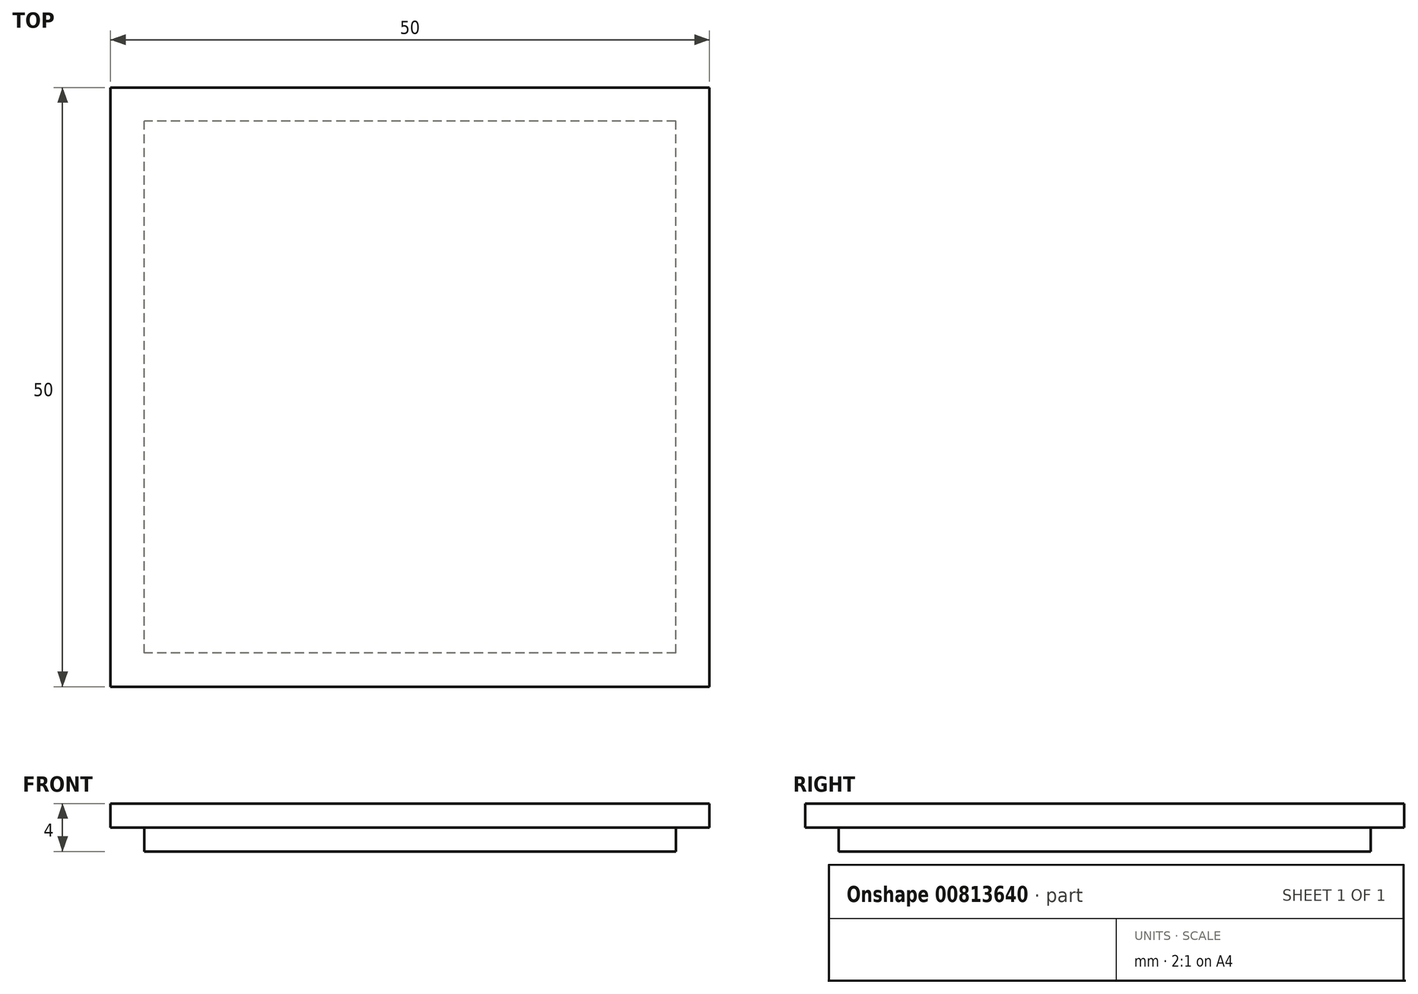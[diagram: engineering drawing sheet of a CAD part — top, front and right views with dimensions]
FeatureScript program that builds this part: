
annotation { "Feature Type Name" : "Feature", "Feature Type Description" : "" }
export const myFeature = defineFeature(function(context is Context, id is Id, definition is map)
    precondition{}
    {
        {
            var Q0;
            Q0=qCreatedBy(makeId("Top.planeOp"),FACE);
            var sketch = newSketch(context, id + "F0", { "sketchPlane" : qUnion([Q0])});
            skLineSegment(sketch, "E0.bottom", {"start": v(25, 25) * mm, "end": v(-25, 25) * mm});
            skLineSegment(sketch, "E0.top", {"start": v(25, -25) * mm, "end": v(-25, -25) * mm});
            skLineSegment(sketch, "E0.left", {"start": v(25, 25) * mm, "end": v(25, -25) * mm});
            skLineSegment(sketch, "E0.right", {"start": v(-25, 25) * mm, "end": v(-25, -25) * mm});
            skPoint(sketch, "E0.middle", {"position": v(0, 0) * mm});
            skLineSegment(sketch, "E1.bottom", {"start": v(22.2, -22.2) * mm, "end": v(-22.2, -22.2) * mm});
            skLineSegment(sketch, "E1.top", {"start": v(22.2, 22.2) * mm, "end": v(-22.2, 22.2) * mm});
            skLineSegment(sketch, "E1.left", {"start": v(22.2, -22.2) * mm, "end": v(22.2, 22.2) * mm});
            skLineSegment(sketch, "E1.right", {"start": v(-22.2, -22.2) * mm, "end": v(-22.2, 22.2) * mm});
            skSolve(sketch);
        }
        {
            var Q0;
            Q0=makeQuery(id+"F0.imprint","IMPRINT",FACE,{"disambiguationData":[TD([[makeQuery(id+"F0.imprint","IMPRINT",EDGE,{"derivedFrom":sQuery(id+"F0.wireOp",EDGE,"E1.bottom")}),-1.0]])]});
            var Q1;
            Q1=makeQuery(id+"F0.imprint","IMPRINT",FACE,{"disambiguationData":[TD([[makeQuery(id+"F0.imprint","IMPRINT",EDGE,{"derivedFrom":sQuery(id+"F0.wireOp",EDGE,"E0.bottom")}),1.0]])]});
            extrude(context, id + "F1", {"entities" : qUnion([Q0, Q1]), "depth" : 2 * mm, "offsetDistance" : 25 * mm});
        }
        {
            var Q0;
            Q0=makeQuery(id+"F0.imprint","IMPRINT",FACE,{"disambiguationData":[TD([[makeQuery(id+"F0.imprint","IMPRINT",EDGE,{"derivedFrom":sQuery(id+"F0.wireOp",EDGE,"E1.bottom")}),-1.0]])]});
            extrude(context, id + "F2", {"entities" : qUnion([Q0]), "operationType" : NewBodyOperationType.ADD, "oppositeDirection" : true, "depth" : 2 * mm, "offsetDistance" : 25 * mm});
        }
    });
